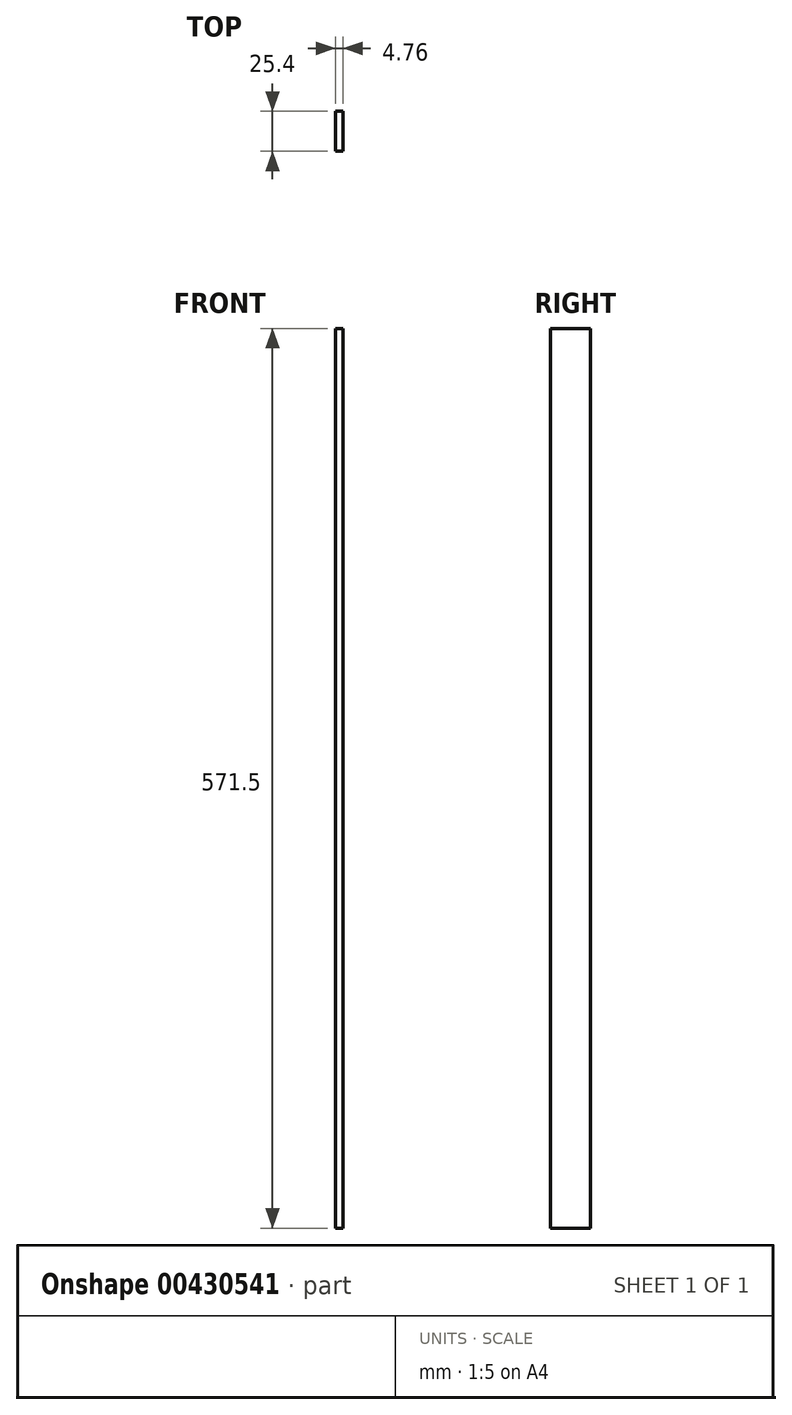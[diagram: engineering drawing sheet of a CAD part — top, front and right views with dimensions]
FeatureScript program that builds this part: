
annotation { "Feature Type Name" : "Feature", "Feature Type Description" : "" }
export const myFeature = defineFeature(function(context is Context, id is Id, definition is map)
    precondition{}
    {
        {
            var Q0;
            Q0=qCreatedBy(makeId("Right.planeOp"),FACE);
            var sketch = newSketch(context, id + "F0", { "sketchPlane" : qUnion([Q0])});
            skLineSegment(sketch, "E0.bottom", {"start": v(-477.67, 282.98) * mm, "end": v(-452.27, 282.98) * mm});
            skLineSegment(sketch, "E0.top", {"start": v(-477.67, -288.52) * mm, "end": v(-452.27, -288.52) * mm});
            skLineSegment(sketch, "E0.left", {"start": v(-477.67, 282.98) * mm, "end": v(-477.67, -288.52) * mm});
            skLineSegment(sketch, "E0.right", {"start": v(-452.27, 282.98) * mm, "end": v(-452.27, -288.52) * mm});
            skSolve(sketch);
        }
        {
            var Q0;
            Q0=makeQuery(id+"F0.imprint","IMPRINT",FACE,{"disambiguationData":[TD([[makeQuery(id+"F0.imprint","IMPRINT",EDGE,{"derivedFrom":sQuery(id+"F0.wireOp",EDGE,"E0.bottom")}),-1.0]])]});
            extrude(context, id + "F1", {"entities" : qUnion([Q0]), "depth" : 4.76 * mm});
        }
    });
